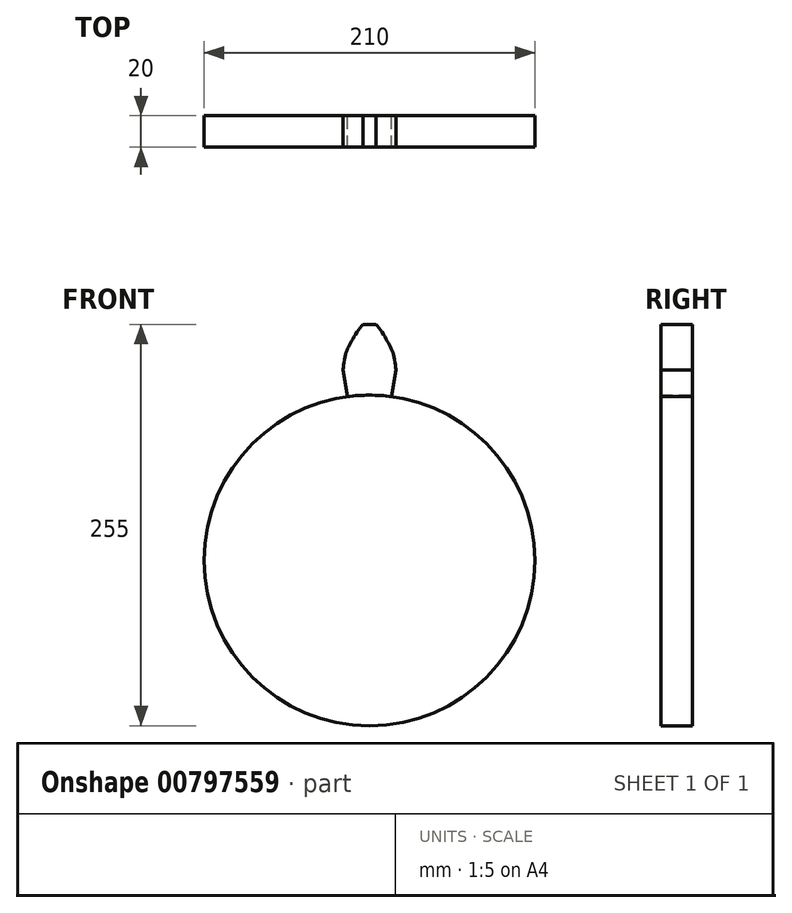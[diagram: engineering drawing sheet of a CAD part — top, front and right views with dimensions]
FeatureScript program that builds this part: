
annotation { "Feature Type Name" : "Feature", "Feature Type Description" : "" }
export const myFeature = defineFeature(function(context is Context, id is Id, definition is map)
    precondition{}
    {
        {
            assignVariable(context, id + "F0", {"name" : "m", "anyValue" : 20});
        }
        {
            var Q0;
            Q0=qCreatedBy(makeId("Front.planeOp"),FACE);
            var sketch = newSketch(context, id + "F1", { "sketchPlane" : qUnion([Q0])});
            skCircle(sketch, "E0", {"center": v(0, 0) * mm, "radius": 105 * mm});
            skCircle(sketch, "E1", {"center": v(0, 0) * mm, "radius": 122.16 * mm, "construction": true});
            skCircle(sketch, "E2", {"center": v(0, 0) * mm, "radius": 130 * mm, "construction": true});
            skCircle(sketch, "E3", {"center": v(0, 0) * mm, "radius": 150 * mm, "construction": true});
            skLineSegment(sketch, "E4", {"start": v(0, 0) * mm, "end": v(27.64, 119) * mm, "construction": true});
            skLineSegment(sketch, "E5", {"start": v(27.64, 119) * mm, "end": v(-15.67, 129.05) * mm, "construction": true});
            skLineSegment(sketch, "E6", {"start": v(-15.67, 129.05) * mm, "end": v(0, 0) * mm, "construction": true});
            skLineSegment(sketch, "E7", {"start": v(0, 0) * mm, "end": v(0, 5.4) * mm});
            skCircle(sketch, "E8", {"center": v(27.64, 119) * mm, "radius": 44.46 * mm, "construction": true});
            skPoint(sketch, "E9", {"position": v(-16.78, 121) * mm});
            skLineSegment(sketch, "E10", {"start": v(0, 0) * mm, "end": v(44.23, 113.87) * mm, "construction": true});
            skLineSegment(sketch, "E11", {"start": v(44.23, 113.87) * mm, "end": v(-13.03, 136.1) * mm, "construction": true});
            skLineSegment(sketch, "E12", {"start": v(-13.03, 136.1) * mm, "end": v(0, 0) * mm, "construction": true});
            skCircle(sketch, "E13", {"center": v(44.23, 113.87) * mm, "radius": 61.42 * mm, "construction": true});
            skLineSegment(sketch, "E14", {"start": v(0, 0) * mm, "end": v(60.23, 106.28) * mm, "construction": true});
            skLineSegment(sketch, "E15", {"start": v(60.23, 106.28) * mm, "end": v(-7.98, 144.93) * mm, "construction": true});
            skLineSegment(sketch, "E16", {"start": v(-7.98, 144.93) * mm, "end": v(0, 0) * mm, "construction": true});
            skCircle(sketch, "E17", {"center": v(60.23, 106.28) * mm, "radius": 78.4 * mm, "construction": true});
            skLineSegment(sketch, "E18", {"start": v(0, 0) * mm, "end": v(68.04, 101.45) * mm, "construction": true});
            skLineSegment(sketch, "E19", {"start": v(68.04, 101.45) * mm, "end": v(-4.25, 149.94) * mm, "construction": true});
            skLineSegment(sketch, "E20", {"start": v(-4.25, 149.94) * mm, "end": v(0, 0) * mm, "construction": true});
            skCircle(sketch, "E21", {"center": v(68.04, 101.45) * mm, "radius": 87.05 * mm, "construction": true});
            skFitSpline(sketch, "E22", {"points": [v(-4.25, 149.94) * mm, v(-7.98, 144.93) * mm, v(-13.03, 136.1) * mm, v(-15.67, 129.05) * mm, v(-16.78, 121) * mm], "startDerivative": vector(-2.47, -2.96) * mm, "endDerivative": vector(-0.23, -3.66) * mm});
            skLineSegment(sketch, "E23", {"start": v(-16.78, 121) * mm, "end": v(-14.05, 104.06) * mm});
            skFitSpline(sketch, "E24.MirrorCS", {"points": [v(4.25, 149.94) * mm, v(7.98, 144.93) * mm, v(13.03, 136.1) * mm, v(15.67, 129.05) * mm, v(16.78, 121) * mm], "startDerivative": vector(2.47, -2.96) * mm, "endDerivative": vector(0.23, -3.66) * mm});
            skLineSegment(sketch, "E25.MirrorCS", {"start": v(16.78, 121) * mm, "end": v(14.05, 104.06) * mm});
            skArc(sketch, "E26", {"start": v(4.25, 149.94) * mm, "mid": v(0, 150) * mm, "end": v(-4.25, 149.94) * mm});
            skSolve(sketch);
        }
        {
            var Q0;
            Q0=makeQuery(id+"F1.imprint","IMPRINT",FACE,{"disambiguationData":[TD([[makeQuery(id+"F1.imprint","IMPRINT",EDGE,{"derivedFrom":sQuery(id+"F1.wireOp",EDGE,"E22")}),1.0]])]});
            extrude(context, id + "F2", {"entities" : qUnion([Q0]), "depth" : (getVariable(context, 'm')) * mm, "offsetDistance" : 25 * mm});
        }
        {
            var Q0;
            Q0=qCreatedBy(makeId("Right.planeOp"),FACE);
            var sketch = newSketch(context, id + "F3", { "sketchPlane" : qUnion([Q0])});
            skLineSegment(sketch, "E27", {"start": v(0, 0) * mm, "end": v(-6.77, 0) * mm});
            skSolve(sketch);
        }
        {
            var Q0;
            {var subQ0=sQuery(id+"F1.wireOp",EDGE,"E0");var subQ1=makeQuery(id+"F1.imprint","INTERSECT",VERTEX,{"derivedFrom":[subQ0,sQuery(id+"F1.wireOp",EDGE,"E23")]});Q0=makeQuery(id+"F1.imprint","IMPRINT",FACE,{"disambiguationData":[TD([[makeQuery(id+"F1.imprint","IMPRINT",EDGE,{"disambiguationData":[TD([[subQ1,1.0]])],"derivedFrom":subQ0}),1.0]])]});}
            extrude(context, id + "F4", {"entities" : qUnion([Q0]), "depth" : (getVariable(context, 'm')) * mm, "offsetDistance" : 25 * mm});
        }
    });
